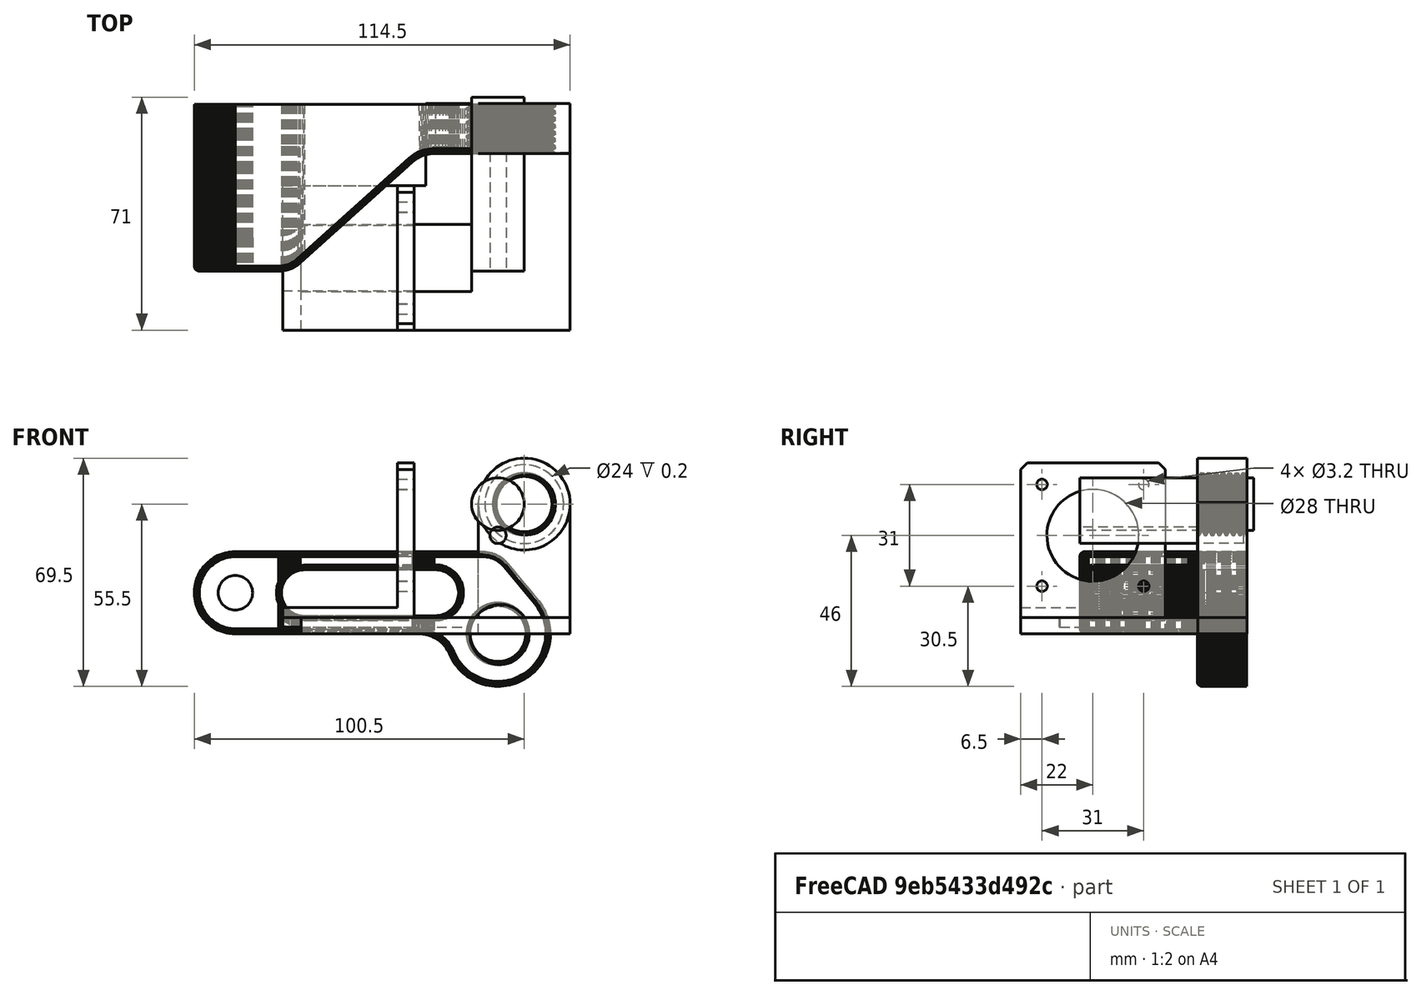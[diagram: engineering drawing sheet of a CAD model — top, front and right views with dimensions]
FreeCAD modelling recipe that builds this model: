
FCSTD DOCUMENT  (FreeCAD 0.18R14555 (Git shallow))
Label: motor-shaft-cutter
License: All rights reserved
LicenseURL: http://en.wikipedia.org/wiki/All_rights_reserved
objects: Part::Cylinder×10, Part::Box×7, Part::MultiFuse×6, Part::Cut×4, Part::Feature×3, Mesh::Feature×1, Part::MultiCommon×1, Part::Chamfer×1
note: 32 computed .brp shape members not serialized (recipe doc carries the construction recipe); baked Part::Feature solids carry a one-line shape summary decoded from their .brp

FEATURE [Mesh::Feature] Guide
FEATURE [Part::Cylinder] Cylinder
  Angle = 360
  AttacherType = Attacher::AttachEngine3D
  Height = 22
  Placement = pos=(0,55,-1.22e-14) rot=(1,0,0;1.5708rad)
  Radius = 14
FEATURE [Part::Feature] Guide001
  shape: bbox 108.5 x 50.8 x 41 mm, 18470 faces, 0 solids (baked)
FEATURE [Part::Feature] Guide001_solid  label="Guide001 (Solid)"
  shape: bbox 108.5 x 50.8 x 41 mm, 18470 faces (baked)
FEATURE [Part::Cylinder] Cylinder001
  Angle = 360
  AttacherType = Attacher::AttachEngine3D
  Height = 50
  Placement = pos=(0,50,30) rot=(1,0,0;1.5708rad)
  Radius = 2.5
FEATURE [Part::Feature] Guide001_solid001  label="Guide001 (Solid)001"
  shape: bbox 108.5 x 50.8 x 41 mm, 16413 faces (baked)
FEATURE [Part::MultiCommon] Common
  Placement = pos=(0,0,39.5) rot=(0,0,1;0rad)
  Shapes = -> [Cylinder,Guide001_solid001]
FEATURE [Part::Box] Box  label="Cube"
  AttacherType = Attacher::AttachEngine3D
  Height = 5
  Length = 44
  Placement = pos=(-22,-22,0) rot=(0,0,1;0rad)
  Width = 44
FEATURE [Part::Cylinder] Cylinder002
  Angle = 360
  AttacherType = Attacher::AttachEngine3D
  Height = 10
  Placement = pos=(-15.5,-15.5,0) rot=(0,0,1;0rad)
  Radius = 1.6
FEATURE [Part::Cylinder] Cylinder003
  Angle = 360
  AttacherType = Attacher::AttachEngine3D
  Height = 10
  Placement = pos=(-15.5,15.5,0) rot=(0,0,1;0rad)
  Radius = 1.6
FEATURE [Part::Cylinder] Cylinder004
  Angle = 360
  AttacherType = Attacher::AttachEngine3D
  Height = 10
  Placement = pos=(15.5,-15.5,0) rot=(0,0,1;0rad)
  Radius = 1.6
FEATURE [Part::Cylinder] Cylinder005
  Angle = 360
  AttacherType = Attacher::AttachEngine3D
  Height = 10
  Placement = pos=(15.5,15.5,0) rot=(0,0,1;0rad)
  Radius = 1.6
FEATURE [Part::MultiFuse] Fusion
  Shapes = -> [Cylinder002,Cylinder003,Cylinder004,Cylinder005]
FEATURE [Part::Cut] Cut
  Base = -> Box
  Tool = -> Fusion
FEATURE [Part::Cylinder] Cylinder006
  Angle = 360
  AttacherType = Attacher::AttachEngine3D
  Height = 10
  Radius = 14
FEATURE [Part::Cut] Cut001
  Base = -> Cut
  Placement = pos=(-9e-16,4,30) rot=(0.57735,-0.57735,0.57735;4.18879rad)
  Tool = -> Cylinder006
FEATURE [Part::Box] Box002  label="Cube002"
  AttacherType = Attacher::AttachEngine3D
  Height = 40
  Length = 28
  Placement = pos=(-14,36,0) rot=(0,0,1;0rad)
  Width = 15
FEATURE [Part::Cylinder] Cylinder007
  Angle = 360
  AttacherType = Attacher::AttachEngine3D
  Height = 15
  Placement = pos=(0,36,39.5) rot=(1,0,0;4.71239rad)
  Radius = 14
FEATURE [Part::Cylinder] Cylinder008
  Angle = 360
  AttacherType = Attacher::AttachEngine3D
  Height = 15
  Placement = pos=(0,36,39.5) rot=(-1,0,0;1.5708rad)
  Radius = 12
FEATURE [Part::Cylinder] Cylinder009
  Angle = 360
  AttacherType = Attacher::AttachEngine3D
  Height = 53
  Placement = pos=(0,53,39.5) rot=(1,0,0;1.5708rad)
  Radius = 8
FEATURE [Part::MultiFuse] Fusion006
  Shapes = -> [Box002,Cylinder007]
FEATURE [Part::Cut] Cut004
  Base = -> Fusion006
  Tool = -> Cylinder008
FEATURE [Part::MultiFuse] Fusion007
  Placement = pos=(8,0,0) rot=(0,0,1;0rad)
  Shapes = -> [Common,Cut004]
FEATURE [Part::Box] Box001  label="Cube001"
  AttacherType = Attacher::AttachEngine3D
  Height = 5
  Length = 44
  Placement = pos=(-22,-18,0) rot=(0,0,1;0rad)
  Width = 69
FEATURE [Part::Box] Box003  label="Cube003"
  AttacherType = Attacher::AttachEngine3D
  Height = 3
  Length = 40
  Placement = pos=(-35,-18,5) rot=(0,0,1;0rad)
  Width = 44
FEATURE [Part::Chamfer] Chamfer
  Base = -> Cut001
  Edges = 2 edges r=2: [Edge1,Edge6]
FEATURE [Part::MultiFuse] Fusion008
  Placement = pos=(-13,0,0) rot=(0,0,1;0rad)
  Shapes = -> [Box003,Chamfer]
FEATURE [Part::Box] Box004  label="Cube004"
  AttacherType = Attacher::AttachEngine3D
  Height = 5
  Length = 38
  Placement = pos=(-60,-18,0) rot=(0,0,1;0rad)
  Width = 44
FEATURE [Part::MultiFuse] Fusion009
  Shapes = -> [Box001,Box004]
FEATURE [Part::Box] Box005  label="Cube005"
  AttacherType = Attacher::AttachEngine3D
  Height = 3
  Length = 52
  Placement = pos=(-60,-6.2,2) rot=(0,0,1;0rad)
  Width = 20.4
FEATURE [Part::Box] Box006  label="Cube006"
  AttacherType = Attacher::AttachEngine3D
  Height = 3
  Length = 40
  Placement = pos=(-48,-6,2) rot=(0,0,1;0rad)
  Width = 20
FEATURE [Part::MultiFuse] Fusion010
  Placement = pos=(-17.6,0,0) rot=(0,0,1;0rad)
  Shapes = -> [Box006,Fusion008]
FEATURE [Part::Cut] Cut005
  Base = -> Fusion009
  Tool = -> Box005
